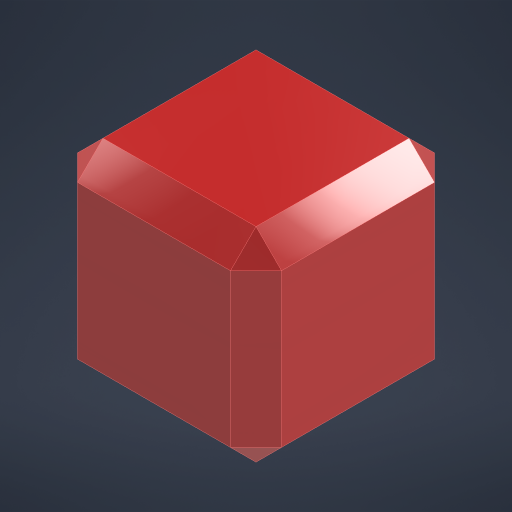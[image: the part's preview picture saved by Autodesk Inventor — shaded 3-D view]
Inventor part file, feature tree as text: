
AUTODESK INVENTOR PART (.ipt)
format: ipt  version: 2023 (Build 270158000, 158)  size: 175,616 bytes
history: native  units: mm
features: extrude x1, chamfer x1, sketch x1
ambient origin geometry x8: Origin, YZ Plane, XZ Plane, XY Plane, X Axis, Y Axis, Z Axis, Center Point
bodies: Solid1 (feature_tree)
feature tree (3):
  extrude  "Extrusion1"  Depth=40.0mm
  chamfer  "Chamfer1"  Distance=40.0mm
  sketch  "Sketch1"  dims[d0=40.0mm d1=40.0mm d2=40.0mm d3=0.0mm d4=5.0mm d5=2.0mm d6=45.0deg]
